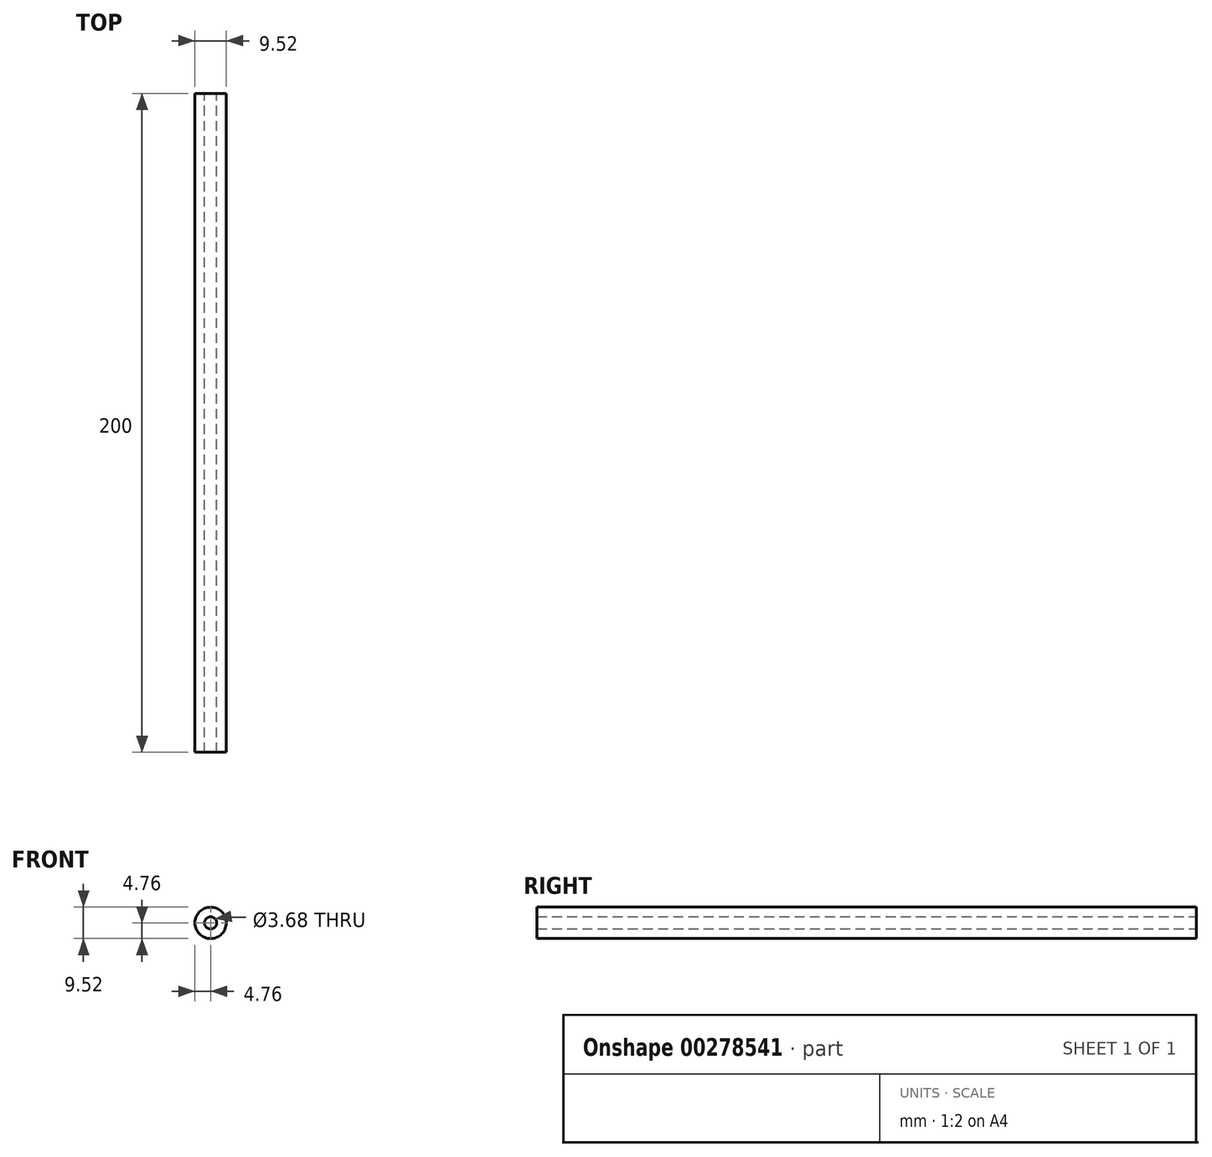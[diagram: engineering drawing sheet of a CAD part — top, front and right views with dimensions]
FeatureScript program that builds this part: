
annotation { "Feature Type Name" : "Feature", "Feature Type Description" : "" }
export const myFeature = defineFeature(function(context is Context, id is Id, definition is map)
    precondition{}
    {
        {
            var Q0;
            Q0=qCreatedBy(makeId("Front.planeOp"),FACE);
            var sketch = newSketch(context, id + "F0", { "sketchPlane" : qUnion([Q0])});
            skCircle(sketch, "E0", {"center": v(0, 0) * mm, "radius": 4.76 * mm});
            skCircle(sketch, "E1", {"center": v(0, 0) * mm, "radius": 1.84 * mm});
            skSolve(sketch);
        }
        {
            var Q0;
            Q0=qSketchRegion(id+"F0",true);
            var Q1;
            Q1=sQuery(id+"F0.wireOp",EDGE,"E0");
            extrude(context, id + "F1", {"entities" : qUnion([Q0]), "surfaceEntities" : qUnion([Q1]), "depth" : 200 * mm});
        }
    });
